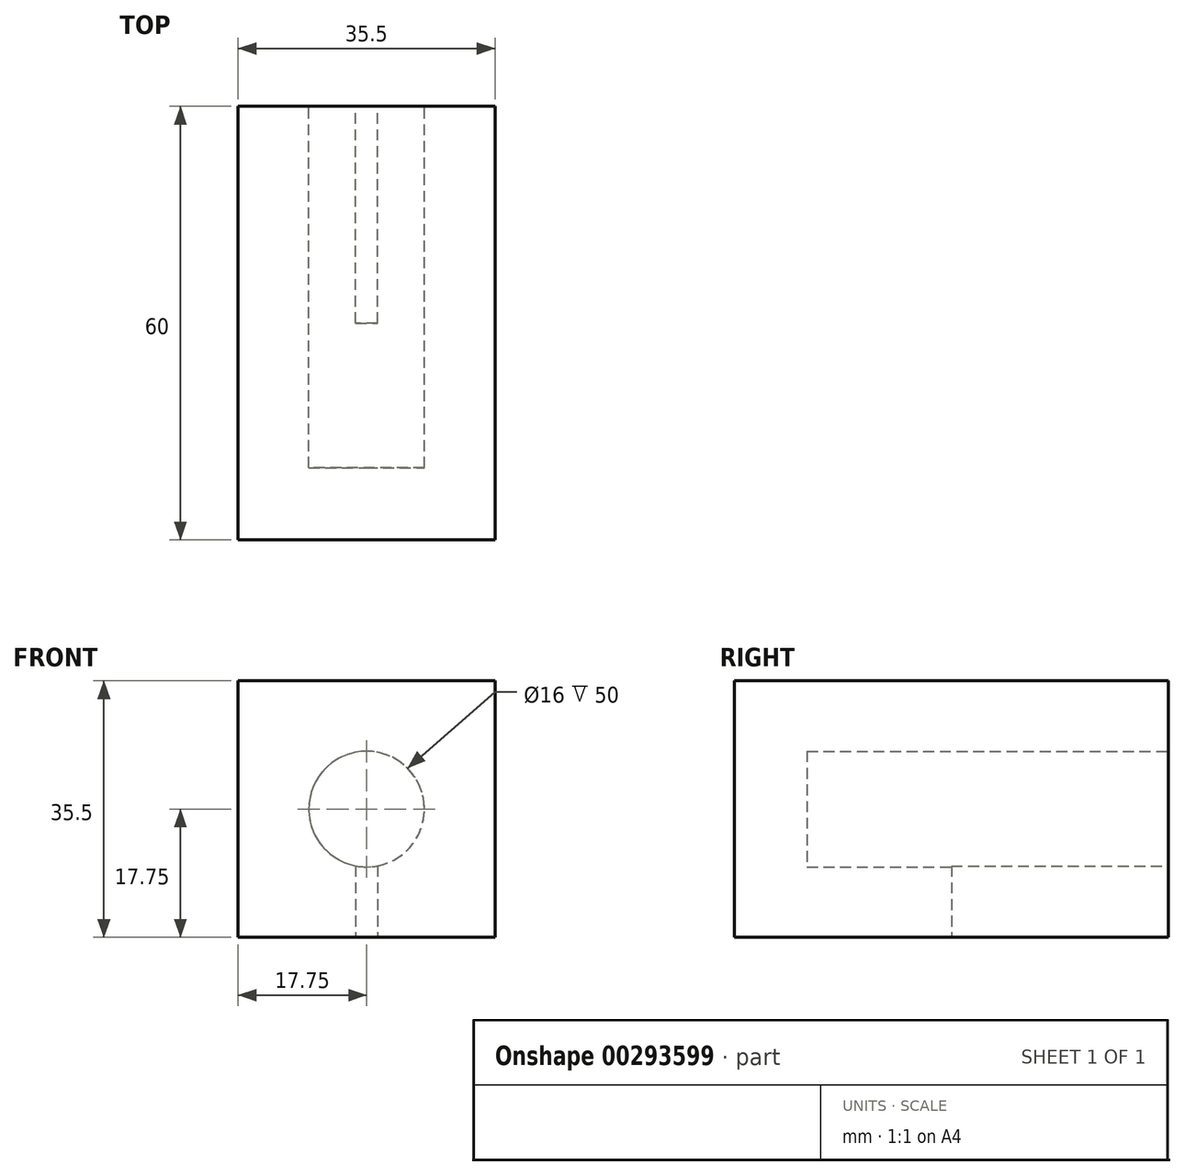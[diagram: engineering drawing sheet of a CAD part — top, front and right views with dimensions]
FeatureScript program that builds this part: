
annotation { "Feature Type Name" : "Feature", "Feature Type Description" : "" }
export const myFeature = defineFeature(function(context is Context, id is Id, definition is map)
    precondition{}
    {
        {
            var Q0;
            Q0=qCreatedBy(makeId("Front.planeOp"),FACE);
            var sketch = newSketch(context, id + "F0", { "sketchPlane" : qUnion([Q0])});
            skLineSegment(sketch, "E0.bottom", {"start": v(-17.75, 17.75) * mm, "end": v(17.75, 17.75) * mm});
            skLineSegment(sketch, "E0.top", {"start": v(-17.75, -17.75) * mm, "end": v(17.75, -17.75) * mm});
            skLineSegment(sketch, "E0.left", {"start": v(-17.75, 17.75) * mm, "end": v(-17.75, -17.75) * mm});
            skLineSegment(sketch, "E0.right", {"start": v(17.75, 17.75) * mm, "end": v(17.75, -17.75) * mm});
            skPoint(sketch, "E0.middle", {"position": v(0, 0) * mm});
            skSolve(sketch);
        }
        {
            var Q0;
            Q0=makeQuery(id+"F0.imprint","IMPRINT",FACE,{"disambiguationData":[TD([[makeQuery(id+"F0.imprint","IMPRINT",EDGE,{"derivedFrom":sQuery(id+"F0.wireOp",EDGE,"E0.bottom")}),-1.0]])]});
            extrude(context, id + "F1", {"entities" : qUnion([Q0]), "depth" : 60 * mm});
        }
        {
            var Q0;
            Q0=makeQuery(id+"F1.opExtrude","CAP_FACE",FACE,{"disambiguationData":[OSD([sQuery(id+"F0.wireOp",EDGE,"E0.bottom"),sQuery(id+"F0.wireOp",EDGE,"E0.top"),sQuery(id+"F0.wireOp",EDGE,"E0.left"),sQuery(id+"F0.wireOp",EDGE,"E0.right")])],"isStart":true});
            var sketch = newSketch(context, id + "F2", { "sketchPlane" : qUnion([Q0])});
            skCircle(sketch, "E1", {"center": v(0, 0) * mm, "radius": 8 * mm});
            skLineSegment(sketch, "E2", {"start": v(0, 24.44) * mm, "end": v(0, -23.29) * mm, "construction": true});
            skSolve(sketch);
        }
        {
            var Q0;
            Q0=makeQuery(id+"F2.imprint","IMPRINT",FACE,{"disambiguationData":[TD([[makeQuery(id+"F2.imprint","IMPRINT",EDGE,{"derivedFrom":sQuery(id+"F2.wireOp",EDGE,"E1")}),1.0]])]});
            extrude(context, id + "F3", {"entities" : qUnion([Q0]), "operationType" : NewBodyOperationType.REMOVE, "oppositeDirection" : true, "depth" : 50 * mm});
        }
        {
            var Q0;
            Q0=makeQuery(id+"F1.opExtrude","CAP_FACE",FACE,{"disambiguationData":[OSD([sQuery(id+"F0.wireOp",EDGE,"E0.bottom"),sQuery(id+"F0.wireOp",EDGE,"E0.top"),sQuery(id+"F0.wireOp",EDGE,"E0.left"),sQuery(id+"F0.wireOp",EDGE,"E0.right")])],"isStart":true});
            var sketch = newSketch(context, id + "F4", { "sketchPlane" : qUnion([Q0])});
            skLineSegment(sketch, "E3", {"start": v(-1.5, -7.86) * mm, "end": v(-1.5, -17.75) * mm});
            skLineSegment(sketch, "E4", {"start": v(0, 0) * mm, "end": v(0, -9.59) * mm, "construction": true});
            skLineSegment(sketch, "E5.MirrorCS", {"start": v(1.5, -7.86) * mm, "end": v(1.5, -17.75) * mm});
            skLineSegment(sketch, "E6.0", {"start": v(17.75, -17.75) * mm, "end": v(-17.75, -17.75) * mm});
            skArc(sketch, "E7.0", {"start": v(1.5, -7.86) * mm, "mid": v(0, 8) * mm, "end": v(-1.5, -7.86) * mm});
            skPoint(sketch, "E8.orphan", {"position": v(-1.5, -1.9) * mm});
            skPoint(sketch, "E9.orphan", {"position": v(1.5, -1.9) * mm});
            skPoint(sketch, "E10.orphan", {"position": v(1.5, -21.12) * mm});
            skPoint(sketch, "E11.orphan", {"position": v(-1.5, -21.12) * mm});
            skSolve(sketch);
        }
        {
            var Q0;
            {var subQ0=sQuery(id+"F4.wireOp",EDGE,"E3");Q0=makeQuery(id+"F4.imprint","IMPRINT",FACE,{"disambiguationData":[TD([[makeQuery(id+"F4.imprint","IMPRINT",EDGE,{"derivedFrom":subQ0}),1.0]])]});}
            extrude(context, id + "F5", {"entities" : qUnion([Q0]), "operationType" : NewBodyOperationType.REMOVE, "oppositeDirection" : true, "depth" : 30 * mm});
        }
    });
